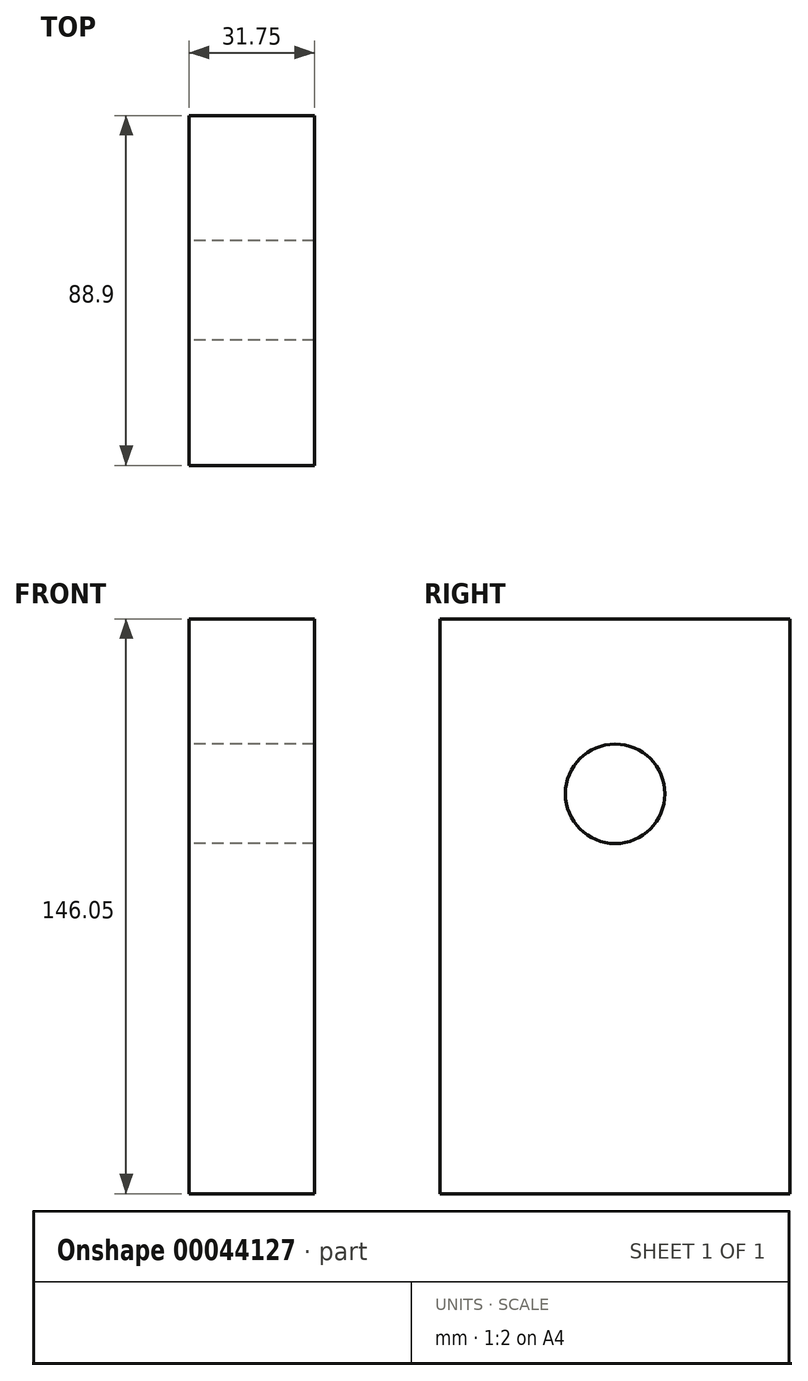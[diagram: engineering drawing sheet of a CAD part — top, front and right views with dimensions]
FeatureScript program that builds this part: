
annotation { "Feature Type Name" : "Feature", "Feature Type Description" : "" }
export const myFeature = defineFeature(function(context is Context, id is Id, definition is map)
    precondition{}
    {
        {
            var Q0;
            Q0=qCreatedBy(makeId("Right.planeOp"),FACE);
            var sketch = newSketch(context, id + "F0", { "sketchPlane" : qUnion([Q0])});
            skLineSegment(sketch, "E0.bottom", {"start": v(0, 0) * mm, "end": v(203.2, 0) * mm, "construction": true});
            skLineSegment(sketch, "E0.top", {"start": v(0, 19.05) * mm, "end": v(203.2, 19.05) * mm, "construction": true});
            skLineSegment(sketch, "E0.left", {"start": v(0, 0) * mm, "end": v(0, 19.05) * mm, "construction": true});
            skLineSegment(sketch, "E0.right", {"start": v(203.2, 0) * mm, "end": v(203.2, 19.05) * mm, "construction": true});
            skLineSegment(sketch, "E1.bottom", {"start": v(203.2, 19.05) * mm, "end": v(165.1, 19.05) * mm, "construction": true});
            skLineSegment(sketch, "E1.top", {"start": v(203.2, 107.95) * mm, "end": v(165.1, 107.95) * mm, "construction": true});
            skLineSegment(sketch, "E1.left", {"start": v(203.2, 19.05) * mm, "end": v(203.2, 107.95) * mm, "construction": true});
            skLineSegment(sketch, "E1.right", {"start": v(165.1, 19.05) * mm, "end": v(165.1, 107.95) * mm, "construction": true});
            skLineSegment(sketch, "E2.bottom", {"start": v(0, 19.05) * mm, "end": v(88.9, 19.05) * mm, "construction": true});
            skLineSegment(sketch, "E2.top", {"start": v(0, 165.1) * mm, "end": v(88.9, 165.1) * mm, "construction": true});
            skLineSegment(sketch, "E2.left", {"start": v(0, 19.05) * mm, "end": v(0, 165.1) * mm, "construction": true});
            skLineSegment(sketch, "E2.right", {"start": v(88.9, 19.05) * mm, "end": v(88.9, 165.1) * mm, "construction": true});
            skCircle(sketch, "E3", {"center": v(44.45, 120.65) * mm, "radius": 12.7 * mm, "construction": true});
            skPoint(sketch, "E3.centerSnap0", {"position": v(44.45, 165.1) * mm});
            skLineSegment(sketch, "E4.bottom", {"start": v(88.9, 165.1) * mm, "end": v(0, 165.1) * mm});
            skLineSegment(sketch, "E4.top", {"start": v(88.9, 19.05) * mm, "end": v(0, 19.05) * mm});
            skLineSegment(sketch, "E4.left", {"start": v(88.9, 165.1) * mm, "end": v(88.9, 19.05) * mm});
            skLineSegment(sketch, "E4.right", {"start": v(0, 165.1) * mm, "end": v(0, 19.05) * mm});
            skCircle(sketch, "E5", {"center": v(44.45, 120.65) * mm, "radius": 12.63 * mm});
            skSolve(sketch);
        }
        {
            var Q0;
            Q0 = qSketchRegion(id + "F0", true);
            extrude(context, id + "F1", {"entities" : qUnion([Q0]), "depth" : 31.75 * mm});
        }
    });
